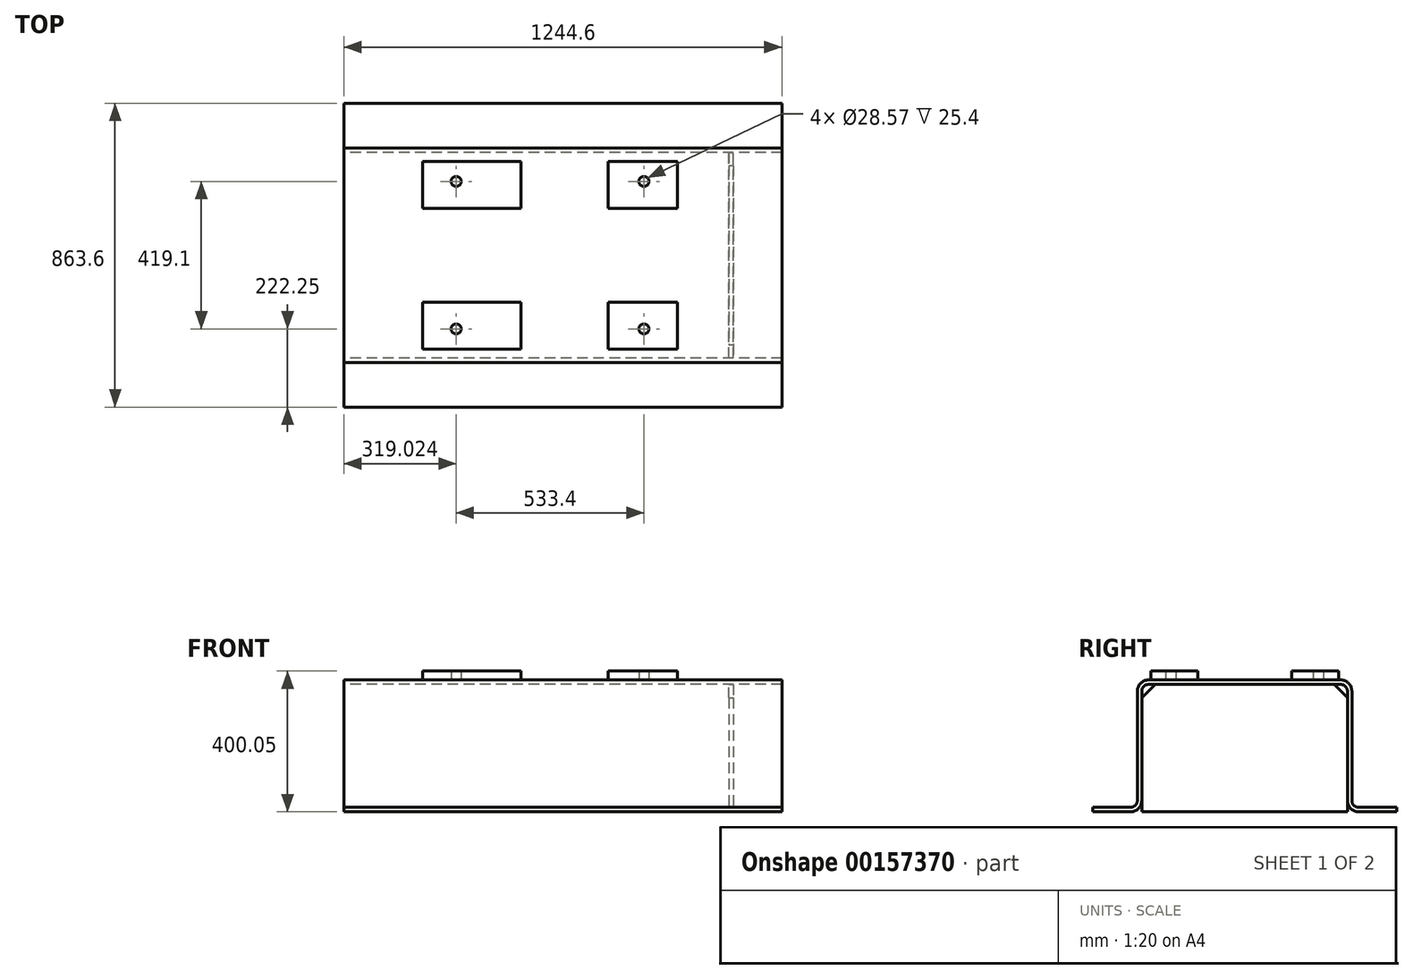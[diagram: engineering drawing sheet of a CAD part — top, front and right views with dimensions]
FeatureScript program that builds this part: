
annotation { "Feature Type Name" : "Feature", "Feature Type Description" : "" }
export const myFeature = defineFeature(function(context is Context, id is Id, definition is map)
    precondition{}
    {
        {
            var Q0;
            Q0=qCreatedBy(makeId("Right.planeOp"),FACE);
            var sketch = newSketch(context, id + "F0", { "sketchPlane" : qUnion([Q0])});
            skLineSegment(sketch, "E0", {"start": v(323.85, 0) * mm, "end": v(431.8, 0) * mm});
            skLineSegment(sketch, "E1", {"start": v(0, 389.85) * mm, "end": v(0, -350.8) * mm, "construction": true});
            skLineSegment(sketch, "E2.0", {"start": v(323.85, 12.7) * mm, "end": v(431.8, 12.7) * mm});
            skLineSegment(sketch, "E3.0", {"start": v(0, 374.65) * mm, "end": v(273.05, 374.65) * mm});
            skLineSegment(sketch, "E4.0", {"start": v(304.8, 342.9) * mm, "end": v(304.8, 31.75) * mm});
            skLineSegment(sketch, "E5.0", {"start": v(292.1, 342.9) * mm, "end": v(292.1, 31.75) * mm});
            skLineSegment(sketch, "E6.0", {"start": v(0, 361.95) * mm, "end": v(273.05, 361.95) * mm});
            skArc(sketch, "E7.filletArc", {"start": v(304.8, 31.75) * mm, "mid": v(310.38, 18.28) * mm, "end": v(323.85, 12.7) * mm});
            skArc(sketch, "E8.filletArc", {"start": v(292.1, 342.9) * mm, "mid": v(286.52, 356.37) * mm, "end": v(273.05, 361.95) * mm});
            skArc(sketch, "E9.filletArc", {"start": v(304.8, 342.9) * mm, "mid": v(295.5, 365.35) * mm, "end": v(273.05, 374.65) * mm});
            skPoint(sketch, "E10.newPointB", {"position": v(-431.8, 0) * mm});
            skArc(sketch, "E10.filletArc", {"start": v(292.1, 31.75) * mm, "mid": v(301.4, 9.3) * mm, "end": v(323.85, 0) * mm});
            skLineSegment(sketch, "E11", {"start": v(431.8, 12.7) * mm, "end": v(431.8, 0) * mm});
            skLineSegment(sketch, "E12.MirrorCS", {"start": v(-431.8, 12.7) * mm, "end": v(-431.8, 0) * mm});
            skArc(sketch, "E13.MirrorCS", {"start": v(-292.1, 342.9) * mm, "mid": v(-286.52, 356.37) * mm, "end": v(-273.05, 361.95) * mm});
            skArc(sketch, "E14.MirrorCS", {"start": v(-304.8, 31.75) * mm, "mid": v(-310.38, 18.28) * mm, "end": v(-323.85, 12.7) * mm});
            skArc(sketch, "E15.MirrorCS", {"start": v(-292.1, 31.75) * mm, "mid": v(-301.4, 9.3) * mm, "end": v(-323.85, 0) * mm});
            skLineSegment(sketch, "E16.MirrorCS", {"start": v(-323.85, 0) * mm, "end": v(-431.8, 0) * mm});
            skArc(sketch, "E17.MirrorCS", {"start": v(-304.8, 342.9) * mm, "mid": v(-295.5, 365.35) * mm, "end": v(-273.05, 374.65) * mm});
            skLineSegment(sketch, "E18.MirrorCS", {"start": v(0, 361.95) * mm, "end": v(-273.05, 361.95) * mm});
            skLineSegment(sketch, "E19.MirrorCS", {"start": v(-323.85, 12.7) * mm, "end": v(-431.8, 12.7) * mm});
            skLineSegment(sketch, "E20.MirrorCS", {"start": v(-292.1, 342.9) * mm, "end": v(-292.1, 31.75) * mm});
            skLineSegment(sketch, "E21.MirrorCS", {"start": v(0, 374.65) * mm, "end": v(-273.05, 374.65) * mm});
            skLineSegment(sketch, "E22.MirrorCS", {"start": v(-304.8, 342.9) * mm, "end": v(-304.8, 31.75) * mm});
            skSolve(sketch);
        }
        {
            var Q0;
            Q0=qSketchRegion(id+"F0",true);
            extrude(context, id + "F1", {"entities" : qUnion([Q0]), "endBound" : BoundingType.SYMMETRIC, "depth" : 1244.6 * mm});
        }
        {
            var Q0;
            Q0=makeQuery(id+"F1.opExtrude","SWEPT_FACE",FACE,{"disambiguationData":[OSD([sQuery(id+"F0.wireOp",EDGE,"E3.0"),sQuery(id+"F0.wireOp",EDGE,"E21.MirrorCS")])]});
            var sketch = newSketch(context, id + "F2", { "sketchPlane" : qUnion([Q0])});
            skLineSegment(sketch, "E23.0", {"start": v(622.3, -273.05) * mm, "end": v(622.3, 273.05) * mm, "construction": true});
            skSolve(sketch);
        }
        {
            var Q0;
            {var subQ0=sQuery(id+"F0.wireOp",EDGE,"E3.0");Q0=makeQuery(id+"F2.imprint","IMPRINT",FACE,{"disambiguationData":[TD([[makeQuery(id+"F2.imprint","IMPRINT",EDGE,{"derivedFrom":makeQuery(id+"F1.opExtrude","SWEPT_EDGE",EDGE,{"disambiguationData":[OSD([subQ0,sQuery(id+"F0.wireOp",EDGE,"E9.filletArc")])]})}),1.0]])]});}
            var sketch = newSketch(context, id + "F3", { "sketchPlane" : qUnion([Q0])});
            skLineSegment(sketch, "E24.0", {"start": v(622.3, -273.05) * mm, "end": v(622.3, 273.05) * mm, "construction": true});
            skLineSegment(sketch, "E25", {"start": v(-721.27, 0) * mm, "end": v(806.54, 0) * mm, "construction": true});
            skLineSegment(sketch, "E26.0", {"start": v(477.77, -273.05) * mm, "end": v(477.77, 273.05) * mm, "construction": true});
            skLineSegment(sketch, "E27.0", {"start": v(-36.58, -273.05) * mm, "end": v(-36.58, 273.05) * mm, "construction": true});
            skLineSegment(sketch, "E28.0", {"start": v(128.52, -273.05) * mm, "end": v(128.52, 273.05) * mm, "construction": true});
            skLineSegment(sketch, "E29.0", {"start": v(325.37, -273.05) * mm, "end": v(325.37, 273.05) * mm, "construction": true});
            skLineSegment(sketch, "E30.0", {"start": v(-721.27, -133.35) * mm, "end": v(806.54, -133.35) * mm, "construction": true});
            skLineSegment(sketch, "E31.0", {"start": v(-721.27, -266.7) * mm, "end": v(806.54, -266.7) * mm, "construction": true});
            skLineSegment(sketch, "E32.bottom", {"start": v(128.52, -133.35) * mm, "end": v(325.37, -133.35) * mm});
            skLineSegment(sketch, "E32.top", {"start": v(128.52, -266.7) * mm, "end": v(325.37, -266.7) * mm});
            skLineSegment(sketch, "E32.left", {"start": v(128.52, -133.35) * mm, "end": v(128.52, -266.7) * mm});
            skLineSegment(sketch, "E32.right", {"start": v(325.37, -133.35) * mm, "end": v(325.37, -266.7) * mm});
            skLineSegment(sketch, "E33.0", {"start": v(-119.13, -273.05) * mm, "end": v(-119.13, 273.05) * mm, "construction": true});
            skLineSegment(sketch, "E34.bottom", {"start": v(-119.13, -266.7) * mm, "end": v(-398.53, -266.7) * mm});
            skLineSegment(sketch, "E34.top", {"start": v(-119.13, -133.35) * mm, "end": v(-398.53, -133.35) * mm});
            skLineSegment(sketch, "E34.left", {"start": v(-119.13, -266.7) * mm, "end": v(-119.13, -133.35) * mm});
            skLineSegment(sketch, "E34.right", {"start": v(-398.53, -266.7) * mm, "end": v(-398.53, -133.35) * mm});
            skLineSegment(sketch, "E35.0", {"start": v(-303.28, -273.05) * mm, "end": v(-303.28, 273.05) * mm, "construction": true});
            skLineSegment(sketch, "E36.0", {"start": v(230.12, -273.05) * mm, "end": v(230.12, 273.05) * mm, "construction": true});
            skLineSegment(sketch, "E37.0", {"start": v(-721.27, -209.55) * mm, "end": v(806.54, -209.55) * mm, "construction": true});
            skCircle(sketch, "E38", {"center": v(-303.28, -209.55) * mm, "radius": 14.29 * mm});
            skCircle(sketch, "E39", {"center": v(230.12, -209.55) * mm, "radius": 14.29 * mm});
            skCircle(sketch, "E40.MirrorC", {"center": v(-303.28, 209.55) * mm, "radius": 14.29 * mm});
            skCircle(sketch, "E41.MirrorC", {"center": v(230.12, 209.55) * mm, "radius": 14.29 * mm});
            skLineSegment(sketch, "E42.MirrorCS", {"start": v(-119.13, 266.7) * mm, "end": v(-398.53, 266.7) * mm});
            skLineSegment(sketch, "E43.MirrorCS", {"start": v(-119.13, 133.35) * mm, "end": v(-398.53, 133.35) * mm});
            skLineSegment(sketch, "E44.MirrorCS", {"start": v(-119.13, 266.7) * mm, "end": v(-119.13, 133.35) * mm});
            skLineSegment(sketch, "E45.MirrorCS", {"start": v(-398.53, 266.7) * mm, "end": v(-398.53, 133.35) * mm});
            skLineSegment(sketch, "E46.MirrorCS", {"start": v(325.37, 133.35) * mm, "end": v(325.37, 266.7) * mm});
            skLineSegment(sketch, "E47.MirrorCS", {"start": v(128.52, 133.35) * mm, "end": v(325.37, 133.35) * mm});
            skLineSegment(sketch, "E48.MirrorCS", {"start": v(128.52, 133.35) * mm, "end": v(128.52, 266.7) * mm});
            skLineSegment(sketch, "E49.MirrorCS", {"start": v(128.52, 266.7) * mm, "end": v(325.37, 266.7) * mm});
            skSolve(sketch);
        }
        {
            var Q0;
            Q0=qSketchRegion(id+"F3",true);
            extrude(context, id + "F4", {"entities" : qUnion([Q0]), "operationType" : NewBodyOperationType.ADD, "depth" : 25.4 * mm});
        }
        {
            var Q0;
            Q0=makeQuery(id+"F1.opExtrude","SWEPT_FACE",FACE,{"disambiguationData":[OSD([sQuery(id+"F0.wireOp",EDGE,"E0")])]});
            var sketch = newSketch(context, id + "F5", { "sketchPlane" : qUnion([Q0])});
            skLineSegment(sketch, "E50.0", {"start": v(477.77, 273.05) * mm, "end": v(477.77, -273.05) * mm, "construction": true});
            skLineSegment(sketch, "E51.0.1", {"start": v(-622.3, -292.1) * mm, "end": v(622.3, -292.1) * mm, "construction": true});
            skLineSegment(sketch, "E51.0.3", {"start": v(622.3, -292.1) * mm, "end": v(-622.3, -292.1) * mm, "construction": true});
            skLineSegment(sketch, "E52.0.1", {"start": v(-622.3, 292.1) * mm, "end": v(622.3, 292.1) * mm, "construction": true});
            skLineSegment(sketch, "E52.0.3", {"start": v(622.3, 292.1) * mm, "end": v(-622.3, 292.1) * mm, "construction": true});
            skLineSegment(sketch, "E53.0", {"start": v(484.12, 292.1) * mm, "end": v(484.12, -292.1) * mm});
            skLineSegment(sketch, "E54.bottom", {"start": v(484.12, 292.1) * mm, "end": v(471.42, 292.1) * mm});
            skLineSegment(sketch, "E54.top", {"start": v(484.12, -292.1) * mm, "end": v(471.42, -292.1) * mm});
            skLineSegment(sketch, "E54.right", {"start": v(471.42, 292.1) * mm, "end": v(471.42, -292.1) * mm});
            skSolve(sketch);
        }
        {
            var Q0;
            Q0=qSketchRegion(id+"F5",true);
            var Q1;
            Q1=makeQuery(id+"F1.opExtrude","SWEPT_FACE",FACE,{"disambiguationData":[OSD([sQuery(id+"F0.wireOp",EDGE,"E6.0"),sQuery(id+"F0.wireOp",EDGE,"E18.MirrorCS")])]});
            extrude(context, id + "F6", {"entities" : qUnion([Q0]), "endBound" : BoundingType.UP_TO_SURFACE, "oppositeDirection" : true, "endBoundEntityFace" : qUnion([Q1]), "depth" : 25.4 * mm});
        }
        {
            var Q0;
            Q0=makeQuery(id+"F6.opExtrude","CAP_EDGE",EDGE,{"disambiguationData":[OSD([sQuery(id+"F5.wireOp",EDGE,"E54.bottom")])],"isStart":false});
            var Q1;
            Q1=makeQuery(id+"F6.opExtrude","CAP_EDGE",EDGE,{"disambiguationData":[OSD([sQuery(id+"F5.wireOp",EDGE,"E54.top")])],"isStart":false});
            chamfer(context, id + "F7", {"entities" : qUnion([Q0, Q1]), "width" : 38.1 * mm, "tangentPropagation" : true});
        }
    });
